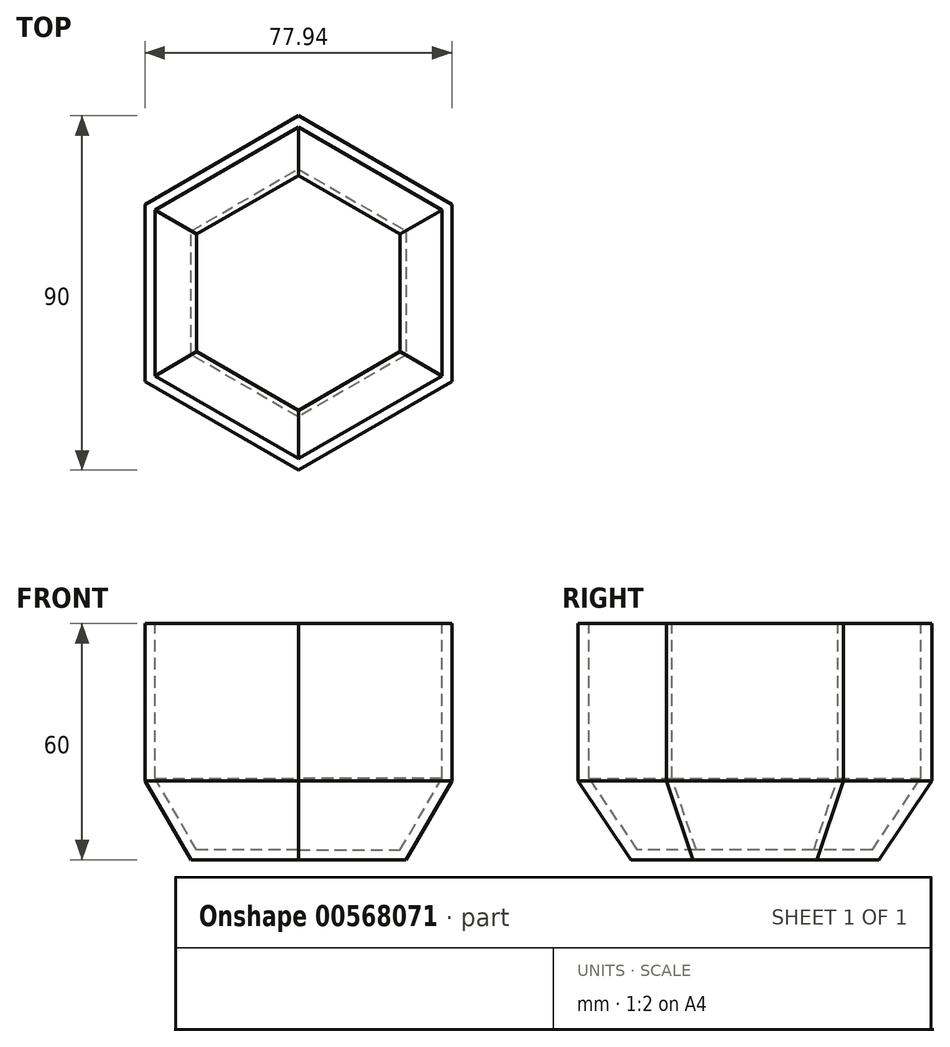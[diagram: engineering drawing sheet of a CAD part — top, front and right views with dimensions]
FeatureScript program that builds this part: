
annotation { "Feature Type Name" : "Feature", "Feature Type Description" : "" }
export const myFeature = defineFeature(function(context is Context, id is Id, definition is map)
    precondition{}
    {
        {
            var Q0;
            Q0=qCreatedBy(makeId("Top.planeOp"),FACE);
            var sketch = newSketch(context, id + "F0", { "sketchPlane" : qUnion([Q0])});
            skCircle(sketch, "E0.cCircle", {"center": v(0, 0) * mm, "radius": 31.5 * mm, "construction": true});
            skLineSegment(sketch, "E0.0", {"start": v(0, 31.5) * mm, "end": v(27.28, 15.75) * mm});
            skLineSegment(sketch, "E0.1", {"start": v(27.28, 15.75) * mm, "end": v(27.28, -15.75) * mm});
            skLineSegment(sketch, "E0.2", {"start": v(27.28, -15.75) * mm, "end": v(0, -31.5) * mm});
            skLineSegment(sketch, "E0.3", {"start": v(0, -31.5) * mm, "end": v(-27.28, -15.75) * mm});
            skLineSegment(sketch, "E0.4", {"start": v(-27.28, -15.75) * mm, "end": v(-27.28, 15.75) * mm});
            skLineSegment(sketch, "E0.5", {"start": v(-27.28, 15.75) * mm, "end": v(0, 31.5) * mm});
            skSolve(sketch);
        }
        {
            var Q0;
            Q0=makeQuery(id+"F0.imprint","IMPRINT",FACE,{"disambiguationData":[TD([[makeQuery(id+"F0.imprint","IMPRINT",EDGE,{"derivedFrom":sQuery(id+"F0.wireOp",EDGE,"E0.0")}),-1.0]])]});
            cPlane(context, id + "F1", {"entities" : qUnion([Q0]), "cplaneType" : CPlaneType.OFFSET, "offset" : 20 * mm, "width" : 150 * mm, "height" : 150 * mm});
        }
        {
            var Q0;
            Q0=qCreatedBy(id+"F1.planeOp",FACE);
            var sketch = newSketch(context, id + "F2", { "sketchPlane" : qUnion([Q0])});
            skCircle(sketch, "E1.cCircle", {"center": v(0, 0) * mm, "radius": 45 * mm, "construction": true});
            skLineSegment(sketch, "E1.0", {"start": v(0, -45) * mm, "end": v(-38.97, -22.5) * mm});
            skLineSegment(sketch, "E1.1", {"start": v(-38.97, -22.5) * mm, "end": v(-38.97, 22.5) * mm});
            skLineSegment(sketch, "E1.2", {"start": v(-38.97, 22.5) * mm, "end": v(0, 45) * mm});
            skLineSegment(sketch, "E1.3", {"start": v(0, 45) * mm, "end": v(38.97, 22.5) * mm});
            skLineSegment(sketch, "E1.4", {"start": v(38.97, 22.5) * mm, "end": v(38.97, -22.5) * mm});
            skLineSegment(sketch, "E1.5", {"start": v(38.97, -22.5) * mm, "end": v(0, -45) * mm});
            skSolve(sketch);
        }
        {
            var Q0;
            Q0=qCreatedBy(id+"F1.planeOp",FACE);
            cPlane(context, id + "F3", {"entities" : qUnion([Q0]), "cplaneType" : CPlaneType.OFFSET, "offset" : 40 * mm, "width" : 150 * mm, "height" : 150 * mm});
        }
        {
            var Q0;
            Q0=makeQuery(id+"F0.imprint","IMPRINT",FACE,{"disambiguationData":[TD([[makeQuery(id+"F0.imprint","IMPRINT",EDGE,{"derivedFrom":sQuery(id+"F0.wireOp",EDGE,"E0.0")}),-1.0]])]});
            var Q1;
            Q1=makeQuery(id+"F2.imprint","IMPRINT",FACE,{"disambiguationData":[TD([[makeQuery(id+"F2.imprint","IMPRINT",EDGE,{"derivedFrom":sQuery(id+"F2.wireOp",EDGE,"E1.0")}),-1.0]])]});
            loft(context, id + "F4", {"sheetProfilesArray" : [{ "sheetProfileEntities" : qUnion([Q0]) }, { "sheetProfileEntities" : qUnion([Q1]) }]});
        }
        {
            var Q0;
            Q0=makeQuery(id+"F4.opLoft","SWEPT_BODY",BODY,{"disambiguationData":[OSD([makeQuery(id+"F0.imprint","IMPRINT",FACE,{"disambiguationData":[TD([[makeQuery(id+"F0.imprint","IMPRINT",EDGE,{"derivedFrom":sQuery(id+"F0.wireOp",EDGE,"E0.0")}),-1.0]])]}),makeQuery(id+"F2.imprint","IMPRINT",FACE,{"disambiguationData":[TD([[makeQuery(id+"F2.imprint","IMPRINT",EDGE,{"derivedFrom":sQuery(id+"F2.wireOp",EDGE,"E1.0")}),-1.0]])]})])]});
            transform(context, id + "F5", {"entities" : qUnion([Q0]), "transformType" : TransformType.TRANSLATION_3D, "dx" : 0 * mm, "dy" : 133 * mm, "dz" : 0 * mm, "makeCopy" : true});
        }
        {
            var Q0;
            Q0=qCreatedBy(id+"F3.planeOp",FACE);
            var sketch = newSketch(context, id + "F6", { "sketchPlane" : qUnion([Q0])});
            skCircle(sketch, "E2.cCircle", {"center": v(0, 0) * mm, "radius": 45 * mm, "construction": true});
            skLineSegment(sketch, "E2.0", {"start": v(0, -45) * mm, "end": v(-38.97, -22.5) * mm});
            skLineSegment(sketch, "E2.1", {"start": v(-38.97, -22.5) * mm, "end": v(-38.97, 22.5) * mm});
            skLineSegment(sketch, "E2.2", {"start": v(-38.97, 22.5) * mm, "end": v(0, 45) * mm});
            skLineSegment(sketch, "E2.3", {"start": v(0, 45) * mm, "end": v(38.97, 22.5) * mm});
            skLineSegment(sketch, "E2.4", {"start": v(38.97, 22.5) * mm, "end": v(38.97, -22.5) * mm});
            skLineSegment(sketch, "E2.5", {"start": v(38.97, -22.5) * mm, "end": v(0, -45) * mm});
            skSolve(sketch);
        }
        {
            var Q0;
            Q0=makeQuery(id+"F5.opPattern","COPY",BODY,{"derivedFrom":makeQuery(id+"F4.opLoft","SWEPT_BODY",BODY,{"disambiguationData":[OSD([makeQuery(id+"F0.imprint","IMPRINT",FACE,{"disambiguationData":[TD([[makeQuery(id+"F0.imprint","IMPRINT",EDGE,{"derivedFrom":sQuery(id+"F0.wireOp",EDGE,"E0.0")}),-1.0]])]}),makeQuery(id+"F2.imprint","IMPRINT",FACE,{"disambiguationData":[TD([[makeQuery(id+"F2.imprint","IMPRINT",EDGE,{"derivedFrom":sQuery(id+"F2.wireOp",EDGE,"E1.0")}),-1.0]])]})])]}),"instanceName":"1"});
            deleteBodies(context, id + "F7", {"entities" : qUnion([Q0])});
        }
        {
            var Q1;
            Q1=makeQuery(id+"F4.opLoft","CAP_FACE",FACE,{"disambiguationData":[OSD([makeQuery(id+"F2.imprint","IMPRINT",FACE,{"disambiguationData":[TD([[makeQuery(id+"F2.imprint","IMPRINT",EDGE,{"derivedFrom":sQuery(id+"F2.wireOp",EDGE,"E1.0")}),-1.0]])]})])],"isStart":true});
            var Q2;
            Q2=makeQuery(id+"F6.imprint","IMPRINT",FACE,{"disambiguationData":[TD([[makeQuery(id+"F6.imprint","IMPRINT",EDGE,{"derivedFrom":sQuery(id+"F6.wireOp",EDGE,"E2.0")}),-1.0]])]});
            loft(context, id + "F8", {"operationType" : NewBodyOperationType.ADD, "sheetProfilesArray" : [{ "sheetProfileEntities" : qUnion([Q1]) }, { "sheetProfileEntities" : qUnion([Q2]) }]});
        }
        {
            var Q0;
            Q0=makeQuery(id+"F8.opLoft","CAP_FACE",FACE,{"disambiguationData":[OSD([makeQuery(id+"F6.imprint","IMPRINT",FACE,{"disambiguationData":[TD([[makeQuery(id+"F6.imprint","IMPRINT",EDGE,{"derivedFrom":sQuery(id+"F6.wireOp",EDGE,"E2.0")}),-1.0]])]})])],"isStart":true});
            shell(context, id + "F9", {"entities" : qUnion([Q0]), "thickness" : 2.5 * mm});
        }
    });
